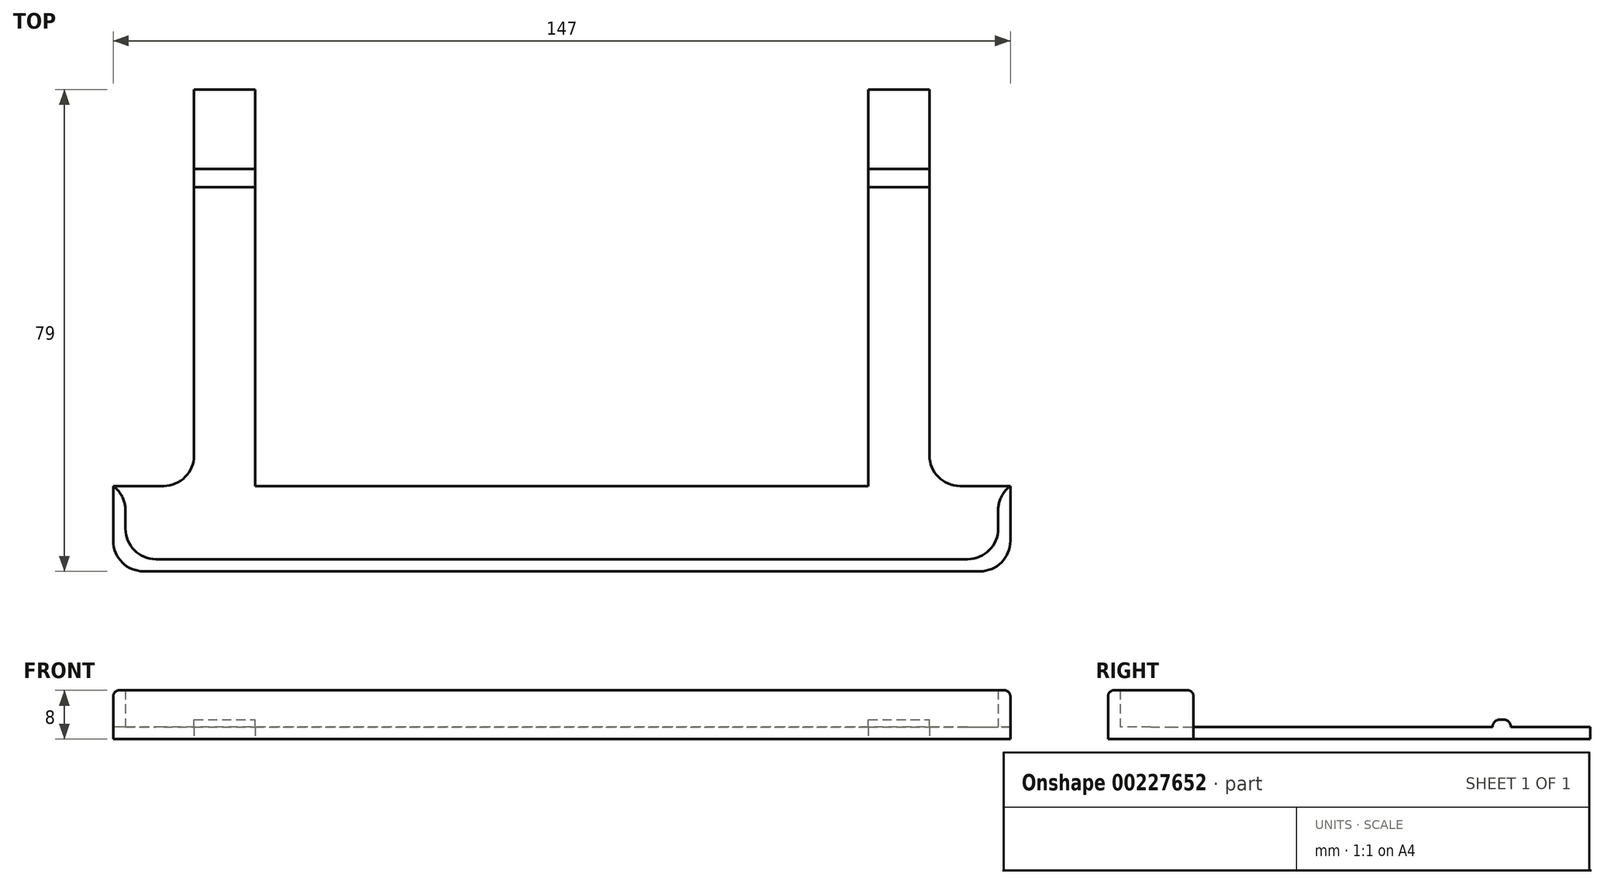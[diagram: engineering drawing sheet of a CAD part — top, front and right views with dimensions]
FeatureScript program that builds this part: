
annotation { "Feature Type Name" : "Feature", "Feature Type Description" : "" }
export const myFeature = defineFeature(function(context is Context, id is Id, definition is map)
    precondition{}
    {
        {
            assignVariable(context, id + "F0", {"name" : "CatchHeight", "anyValue" : 1.2});
        }
        {
            assignVariable(context, id + "F1", {"name" : "WallHeight", "anyValue" : 8});
        }
        {
            var Q0;
            Q0=qCreatedBy(makeId("Top.planeOp"),FACE);
            var sketch = newSketch(context, id + "F2", { "sketchPlane" : qUnion([Q0])});
            skLineSegment(sketch, "E0.bottom", {"start": v(-52.75, 65) * mm, "end": v(-42.75, 65) * mm});
            skLineSegment(sketch, "E0.top", {"start": v(-52.75, 0) * mm, "end": v(-42.75, 0) * mm});
            skLineSegment(sketch, "E0.left", {"start": v(-52.75, 65) * mm, "end": v(-52.75, 0) * mm});
            skLineSegment(sketch, "E0.right", {"start": v(-42.75, 65) * mm, "end": v(-42.75, 0) * mm});
            skLineSegment(sketch, "E1.bottom", {"start": v(57.75, 65) * mm, "end": v(67.75, 65) * mm});
            skLineSegment(sketch, "E1.top", {"start": v(57.75, 0) * mm, "end": v(67.75, 0) * mm});
            skLineSegment(sketch, "E1.left", {"start": v(57.75, 65) * mm, "end": v(57.75, 0) * mm});
            skLineSegment(sketch, "E1.right", {"start": v(67.75, 65) * mm, "end": v(67.75, 0) * mm});
            skLineSegment(sketch, "E2.bottom", {"start": v(-52.75, 0) * mm, "end": v(67.75, 0) * mm});
            skLineSegment(sketch, "E2.top", {"start": v(-52.75, -12) * mm, "end": v(67.75, -12) * mm});
            skLineSegment(sketch, "E2.left", {"start": v(-52.75, 0) * mm, "end": v(-52.75, -12) * mm});
            skLineSegment(sketch, "E2.right", {"start": v(67.75, 0) * mm, "end": v(67.75, -12) * mm});
            skLineSegment(sketch, "E3", {"start": v(-42.75, 0) * mm, "end": v(-42.75, -12) * mm});
            skLineSegment(sketch, "E4", {"start": v(57.75, 0) * mm, "end": v(57.75, -12) * mm});
            skLineSegment(sketch, "E5.bottom", {"start": v(-52.75, 0) * mm, "end": v(-64, 0) * mm});
            skLineSegment(sketch, "E5.top", {"start": v(-52.75, -12) * mm, "end": v(-64, -12) * mm});
            skLineSegment(sketch, "E5.right", {"start": v(-64, 0) * mm, "end": v(-64, -12) * mm});
            skLineSegment(sketch, "E6.bottom", {"start": v(67.75, 0) * mm, "end": v(79, 0) * mm});
            skLineSegment(sketch, "E6.top", {"start": v(67.75, -12) * mm, "end": v(79, -12) * mm});
            skLineSegment(sketch, "E6.right", {"start": v(79, 0) * mm, "end": v(79, -12) * mm});
            skLineSegment(sketch, "E7.bottom", {"start": v(-64, 0) * mm, "end": v(-66, 0) * mm});
            skLineSegment(sketch, "E7.top", {"start": v(-64, -12) * mm, "end": v(-66, -12) * mm});
            skLineSegment(sketch, "E7.right", {"start": v(-66, 0) * mm, "end": v(-66, -12) * mm});
            skLineSegment(sketch, "E8.bottom", {"start": v(79, 0) * mm, "end": v(81, 0) * mm});
            skLineSegment(sketch, "E8.top", {"start": v(79, -12) * mm, "end": v(81, -12) * mm});
            skLineSegment(sketch, "E8.right", {"start": v(81, 0) * mm, "end": v(81, -12) * mm});
            skLineSegment(sketch, "E9.bottom", {"start": v(-66, -12) * mm, "end": v(81, -12) * mm});
            skLineSegment(sketch, "E9.top", {"start": v(-66, -14) * mm, "end": v(81, -14) * mm});
            skLineSegment(sketch, "E9.left", {"start": v(-66, -12) * mm, "end": v(-66, -14) * mm});
            skLineSegment(sketch, "E9.right", {"start": v(81, -12) * mm, "end": v(81, -14) * mm});
            skLineSegment(sketch, "E10.bottom", {"start": v(-42.75, 0) * mm, "end": v(57.75, 0) * mm});
            skLineSegment(sketch, "E10.top", {"start": v(-42.75, -2) * mm, "end": v(57.75, -2) * mm});
            skLineSegment(sketch, "E10.left", {"start": v(-42.75, 0) * mm, "end": v(-42.75, -2) * mm});
            skLineSegment(sketch, "E10.right", {"start": v(57.75, 0) * mm, "end": v(57.75, -2) * mm});
            skSolve(sketch);
        }
        {
            var Q0;
            Q0 = qSketchRegion(id + "F2", true);
            var Q1;
            {var subQ0=sQuery(id+"F2.wireOp",EDGE,"E3");Q1=makeQuery(id+"F2.imprint","IMPRINT",FACE,{"disambiguationData":[TD([[makeQuery(id+"F2.imprint","IMPRINT",EDGE,{"derivedFrom":subQ0}),1.0]])]});}
            var Q2;
            {var subQ0=sQuery(id+"F2.wireOp",EDGE,"E9.bottom");var subQ1=sQuery(id+"F2.wireOp",EDGE,"E5.right");var subQ2=makeQuery(id+"F2.imprint","INTERSECT",VERTEX,{"derivedFrom":[subQ1,subQ0]});Q2=makeQuery(id+"F2.imprint","IMPRINT",FACE,{"disambiguationData":[TD([[makeQuery(id+"F2.imprint","IMPRINT",EDGE,{"disambiguationData":[TD([[subQ2,1.0]])],"derivedFrom":subQ1}),1.0]])]});}
            extrude(context, id + "F3", {"entities" : qUnion([Q0, Q1, Q2]), "depth" : 2 * mm});
        }
        {
            var Q0;
            Q0=makeQuery(id+"F2.imprint","IMPRINT",FACE,{"disambiguationData":[TD([[makeQuery(id+"F2.imprint","IMPRINT",EDGE,{"derivedFrom":sQuery(id+"F2.wireOp",EDGE,"E7.bottom")}),1.0]])]});
            var Q1;
            Q1=makeQuery(id+"F2.imprint","IMPRINT",FACE,{"disambiguationData":[TD([[makeQuery(id+"F2.imprint","IMPRINT",EDGE,{"derivedFrom":sQuery(id+"F2.wireOp",EDGE,"E9.top")}),1.0]])]});
            var Q2;
            Q2=makeQuery(id+"F2.imprint","IMPRINT",FACE,{"disambiguationData":[TD([[makeQuery(id+"F2.imprint","IMPRINT",EDGE,{"derivedFrom":sQuery(id+"F2.wireOp",EDGE,"E8.bottom")}),-1.0]])]});
            var Q3;
            Q3=makeQuery(id+"F2.imprint","IMPRINT",FACE,{"disambiguationData":[TD([[makeQuery(id+"F2.imprint","IMPRINT",EDGE,{"derivedFrom":sQuery(id+"F2.wireOp",EDGE,"E10.bottom")}),-1.0]])]});
            var Q4;
            {var subQ0=sQuery(id+"F2.wireOp",EDGE,"E9.bottom");var subQ1=sQuery(id+"F2.wireOp",EDGE,"E6.right");var subQ2=makeQuery(id+"F2.imprint","INTERSECT",VERTEX,{"derivedFrom":[subQ1,subQ0]});Q4=makeQuery(id+"F2.imprint","IMPRINT",FACE,{"disambiguationData":[TD([[makeQuery(id+"F2.imprint","IMPRINT",EDGE,{"disambiguationData":[TD([[subQ2,1.0]])],"derivedFrom":subQ1}),1.0]])]});}
            var Q5;
            {var subQ0=sQuery(id+"F2.wireOp",EDGE,"E9.bottom");var subQ1=sQuery(id+"F2.wireOp",EDGE,"E5.right");var subQ2=makeQuery(id+"F2.imprint","INTERSECT",VERTEX,{"derivedFrom":[subQ1,subQ0]});Q5=makeQuery(id+"F2.imprint","IMPRINT",FACE,{"disambiguationData":[TD([[makeQuery(id+"F2.imprint","IMPRINT",EDGE,{"disambiguationData":[TD([[subQ2,1.0]])],"derivedFrom":subQ1}),-1.0]])]});}
            extrude(context, id + "F4", {"entities" : qUnion([Q0, Q1, Q2, Q3, Q4, Q5]), "operationType" : NewBodyOperationType.ADD, "depth" : (getVariable(context, 'WallHeight')) * mm});
        }
        {
            var Q0;
            {var subQ0=sQuery(id+"F2.wireOp",EDGE,"E9.left");var subQ1=sQuery(id+"F2.wireOp",EDGE,"E9.top");Q0=makeQuery(id+"F4.boolean.opBoolean","MERGE",EDGE,{"derivedFrom":[makeQuery(id+"F3.opExtrude","SWEPT_EDGE",EDGE,{"disambiguationData":[OSD([subQ1,subQ0])]}),makeQuery(id+"F4.opExtrude","SWEPT_EDGE",EDGE,{"disambiguationData":[OSD([subQ1,subQ0])]})]});}
            var Q1;
            {var subQ0=sQuery(id+"F2.wireOp",EDGE,"E9.right");var subQ1=sQuery(id+"F2.wireOp",EDGE,"E9.top");Q1=makeQuery(id+"F4.boolean.opBoolean","MERGE",EDGE,{"derivedFrom":[makeQuery(id+"F3.opExtrude","SWEPT_EDGE",EDGE,{"disambiguationData":[OSD([subQ1,subQ0])]}),makeQuery(id+"F4.opExtrude","SWEPT_EDGE",EDGE,{"disambiguationData":[OSD([subQ1,subQ0])]})]});}
            var Q2;
            Q2=makeQuery(id+"F4.opExtrude","SWEPT_EDGE",EDGE,{"disambiguationData":[OSD([sQuery(id+"F2.wireOp",EDGE,"E5.right"),sQuery(id+"F2.wireOp",EDGE,"E9.bottom")])]});
            var Q3;
            Q3=makeQuery(id+"F4.opExtrude","SWEPT_EDGE",EDGE,{"disambiguationData":[OSD([sQuery(id+"F2.wireOp",EDGE,"E6.right"),sQuery(id+"F2.wireOp",EDGE,"E9.bottom")])]});
            var Q4;
            Q4=makeQuery(id+"F3.opExtrude","SWEPT_EDGE",EDGE,{"disambiguationData":[OSD([sQuery(id+"F2.wireOp",EDGE,"E6.top"),sQuery(id+"F2.wireOp",EDGE,"E2.right")])]});
            var Q5;
            Q5=makeQuery(id+"F3.opExtrude","SWEPT_EDGE",EDGE,{"disambiguationData":[OSD([sQuery(id+"F2.wireOp",EDGE,"E5.top"),sQuery(id+"F2.wireOp",EDGE,"E2.left")])]});
            fillet(context, id + "F5", {"entities" : qUnion([Q0, Q1, Q2, Q3, Q4, Q5]), "radius" : 5 * mm, "tangentPropagation" : true, "allowEdgeOverflow" : false});
        }
        {
            var Q0;
            Q0=makeQuery(id+"F4.opExtrude","CAP_EDGE",EDGE,{"disambiguationData":[OSD([sQuery(id+"F2.wireOp",EDGE,"E9.top")])],"isStart":false});
            var Q1;
            Q1=makeQuery(id+"F4.opExtrude","CAP_EDGE",EDGE,{"disambiguationData":[OSD([sQuery(id+"F2.wireOp",EDGE,"E9.bottom")])],"isStart":false});
            var Q2;
            Q2=makeQuery(id+"F4.opExtrude","CAP_EDGE",EDGE,{"disambiguationData":[OSD([sQuery(id+"F2.wireOp",EDGE,"E8.bottom")])],"isStart":false});
            var Q3;
            Q3=makeQuery(id+"F4.opExtrude","CAP_EDGE",EDGE,{"disambiguationData":[OSD([sQuery(id+"F2.wireOp",EDGE,"E7.bottom")])],"isStart":false});
            var Q4;
            Q4=makeQuery(id+"F4.opExtrude","CAP_EDGE",EDGE,{"disambiguationData":[OSD([sQuery(id+"F2.wireOp",EDGE,"E10.top")])],"isStart":false});
            var Q5;
            Q5=makeQuery(id+"F4.opExtrude","CAP_EDGE",EDGE,{"disambiguationData":[OSD([sQuery(id+"F2.wireOp",EDGE,"E10.bottom")])],"isStart":false});
            var Q6;
            Q6=makeQuery(id+"F4.opExtrude","CAP_EDGE",EDGE,{"disambiguationData":[OSD([sQuery(id+"F2.wireOp",EDGE,"E10.right")])],"isStart":false});
            var Q7;
            Q7=makeQuery(id+"F4.opExtrude","CAP_EDGE",EDGE,{"disambiguationData":[OSD([sQuery(id+"F2.wireOp",EDGE,"E10.left")])],"isStart":false});
            fillet(context, id + "F6", {"entities" : qUnion([Q0, Q1, Q2, Q3, Q4, Q5, Q6, Q7]), "radius" : 1 * mm, "tangentPropagation" : true, "allowEdgeOverflow" : false});
        }
        {
            var Q0;
            Q0=makeQuery(id+"F3.opExtrude","CAP_FACE",FACE,{"disambiguationData":[OSD([sQuery(id+"F2.wireOp",EDGE,"E0.bottom"),sQuery(id+"F2.wireOp",EDGE,"E0.left"),sQuery(id+"F2.wireOp",EDGE,"E0.right"),sQuery(id+"F2.wireOp",EDGE,"E1.bottom"),sQuery(id+"F2.wireOp",EDGE,"E1.left"),sQuery(id+"F2.wireOp",EDGE,"E1.right"),sQuery(id+"F2.wireOp",EDGE,"E5.bottom"),sQuery(id+"F2.wireOp",EDGE,"E6.bottom"),sQuery(id+"F2.wireOp",EDGE,"E7.bottom"),sQuery(id+"F2.wireOp",EDGE,"E7.right"),sQuery(id+"F2.wireOp",EDGE,"E8.bottom"),sQuery(id+"F2.wireOp",EDGE,"E8.right"),sQuery(id+"F2.wireOp",EDGE,"E9.top"),sQuery(id+"F2.wireOp",EDGE,"E9.left"),sQuery(id+"F2.wireOp",EDGE,"E9.right"),sQuery(id+"F2.wireOp",EDGE,"E10.bottom")])],"isStart":false});
            var sketch = newSketch(context, id + "F7", { "sketchPlane" : qUnion([Q0])});
            skLineSegment(sketch, "E11.bottom", {"start": v(-52.75, 52) * mm, "end": v(-42.75, 52) * mm});
            skLineSegment(sketch, "E11.top", {"start": v(-52.75, 49) * mm, "end": v(-42.75, 49) * mm});
            skLineSegment(sketch, "E11.left", {"start": v(-52.75, 52) * mm, "end": v(-52.75, 49) * mm});
            skLineSegment(sketch, "E11.right", {"start": v(-42.75, 52) * mm, "end": v(-42.75, 49) * mm});
            skLineSegment(sketch, "E12.bottom", {"start": v(57.75, 52) * mm, "end": v(67.75, 52) * mm});
            skLineSegment(sketch, "E12.top", {"start": v(57.75, 49) * mm, "end": v(67.75, 49) * mm});
            skLineSegment(sketch, "E12.left", {"start": v(57.75, 52) * mm, "end": v(57.75, 49) * mm});
            skLineSegment(sketch, "E12.right", {"start": v(67.75, 52) * mm, "end": v(67.75, 49) * mm});
            skSolve(sketch);
        }
        {
            var Q0;
            Q0=makeQuery(id+"F7.imprint","IMPRINT",FACE,{"disambiguationData":[TD([[makeQuery(id+"F7.imprint","IMPRINT",EDGE,{"derivedFrom":sQuery(id+"F7.wireOp",EDGE,"E11.bottom")}),-1.0]])]});
            var Q1;
            Q1=makeQuery(id+"F7.imprint","IMPRINT",FACE,{"disambiguationData":[TD([[makeQuery(id+"F7.imprint","IMPRINT",EDGE,{"derivedFrom":sQuery(id+"F7.wireOp",EDGE,"E12.bottom")}),-1.0]])]});
            extrude(context, id + "F8", {"entities" : qUnion([Q0, Q1]), "operationType" : NewBodyOperationType.ADD, "depth" : (getVariable(context, 'CatchHeight')) * mm});
        }
        {
            var Q0;
            Q0=makeQuery(id+"F8.opExtrude","CAP_EDGE",EDGE,{"disambiguationData":[OSD([sQuery(id+"F7.wireOp",EDGE,"E11.top")])],"isStart":false});
            var Q1;
            Q1=makeQuery(id+"F8.opExtrude","CAP_EDGE",EDGE,{"disambiguationData":[OSD([sQuery(id+"F7.wireOp",EDGE,"E11.bottom")])],"isStart":false});
            var Q2;
            Q2=makeQuery(id+"F8.opExtrude","CAP_EDGE",EDGE,{"disambiguationData":[OSD([sQuery(id+"F7.wireOp",EDGE,"E12.top")])],"isStart":false});
            var Q3;
            Q3=makeQuery(id+"F8.opExtrude","CAP_EDGE",EDGE,{"disambiguationData":[OSD([sQuery(id+"F7.wireOp",EDGE,"E12.bottom")])],"isStart":false});
            fillet(context, id + "F9", {"entities" : qUnion([Q0, Q1, Q2, Q3]), "radius" : 1.2 * mm, "tangentPropagation" : true, "allowEdgeOverflow" : false});
        }
    });
